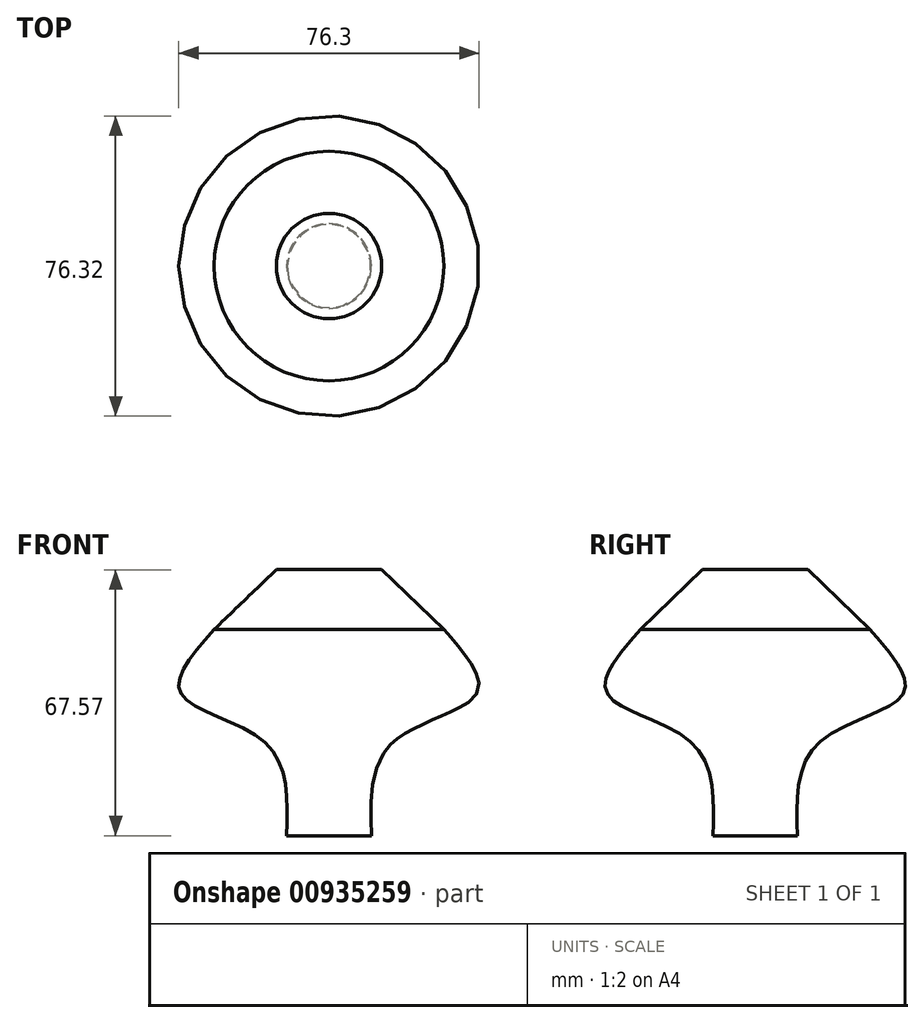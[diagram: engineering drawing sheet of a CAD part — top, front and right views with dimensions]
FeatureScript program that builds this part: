
annotation { "Feature Type Name" : "Feature", "Feature Type Description" : "" }
export const myFeature = defineFeature(function(context is Context, id is Id, definition is map)
    precondition{}
    {
        {
            var Q0;
            Q0=qCreatedBy(makeId("Front.planeOp"),FACE);
            var sketch = newSketch(context, id + "F0", { "sketchPlane" : qUnion([Q0])});
            skLineSegment(sketch, "E0", {"start": v(0, 0) * mm, "end": v(0, 67.57) * mm});
            skLineSegment(sketch, "E1", {"start": v(0, 67.57) * mm, "end": v(13.38, 67.57) * mm});
            skLineSegment(sketch, "E2", {"start": v(13.38, 67.57) * mm, "end": v(29.16, 52.4) * mm});
            skFitSpline(sketch, "E3", {"points": [v(29.16, 52.4) * mm, v(37.66, 36.2) * mm, v(16.21, 23.66) * mm, v(10.75, 0) * mm], "startDerivative": vector(53.13, -60.2) * mm, "endDerivative": vector(2.75, -78.06) * mm});
            skLineSegment(sketch, "E4", {"start": v(10.75, 0) * mm, "end": v(0, 0) * mm});
            skLineSegment(sketch, "E5", {"start": v(10.43, 9.04) * mm, "end": v(12.68, 12.28) * mm, "construction": true});
            skSolve(sketch);
        }
        {
            var Q0;
            Q0=qCreatedBy(makeId("Front.planeOp"),FACE);
            var sketch = newSketch(context, id + "F1", { "sketchPlane" : qUnion([Q0])});
            skLineSegment(sketch, "E6", {"start": v(0, -28.21) * mm, "end": v(0, 98.75) * mm, "construction": true});
            skSolve(sketch);
        }
        {
            var Q0;
            Q0 = qSketchRegion(id + "F0", true);
            var Q1;
            Q1=sQuery(id+"F1.wireOp",EDGE,"E6");
            revolve(context, id + "F2", {"surfaceOperationType" : NewSurfaceOperationType.NEW, "entities" : qUnion([Q0]), "axis" : qUnion([Q1]), "revolveType" : RevolveType.FULL});
        }
    });
